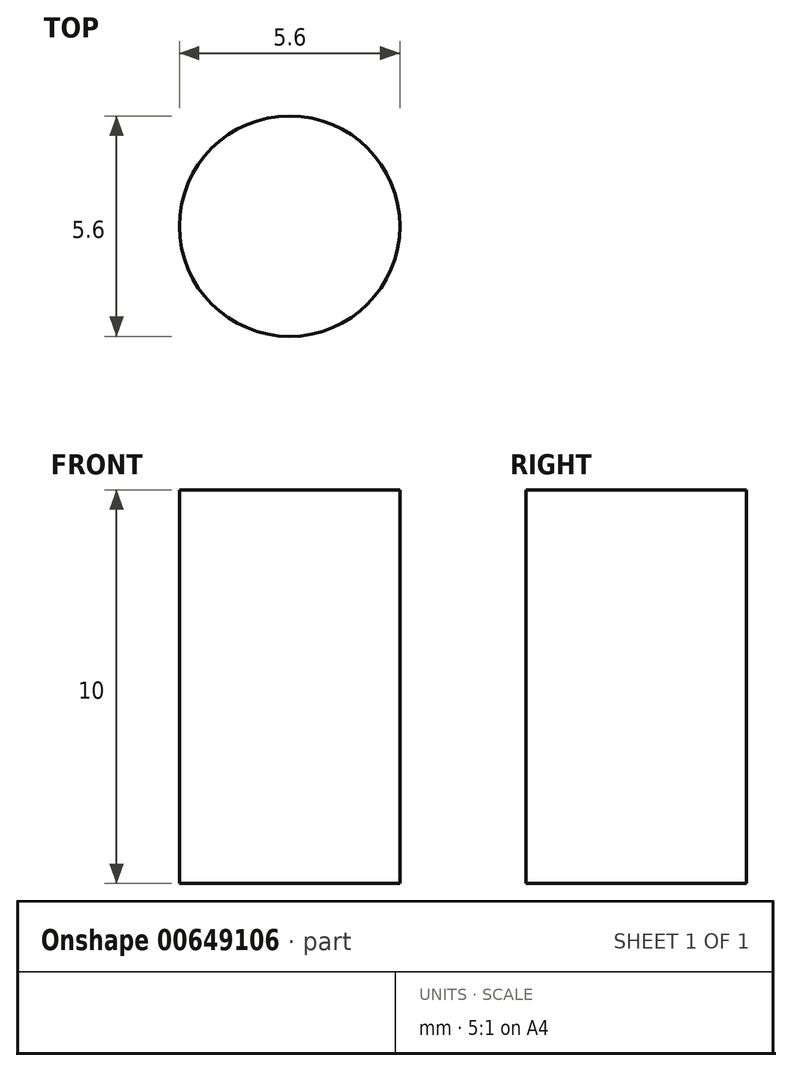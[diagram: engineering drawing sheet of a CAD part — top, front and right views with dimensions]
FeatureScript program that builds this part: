
annotation { "Feature Type Name" : "Feature", "Feature Type Description" : "" }
export const myFeature = defineFeature(function(context is Context, id is Id, definition is map)
    precondition{}
    {
        {
            var Q0;
            Q0=qCreatedBy(makeId("Top.planeOp"),FACE);
            var sketch = newSketch(context, id + "F0", { "sketchPlane" : qUnion([Q0])});
            skCircle(sketch, "E0", {"center": v(0, 0) * mm, "radius": 2.8 * mm});
            skSolve(sketch);
        }
        {
            var Q0;
            Q0=makeQuery(id+"F0.imprint","IMPRINT",FACE,{"disambiguationData":[TD([[makeQuery(id+"F0.imprint","IMPRINT",EDGE,{"derivedFrom":sQuery(id+"F0.wireOp",EDGE,"E0")}),1.0]])]});
            extrude(context, id + "F1", {"entities" : qUnion([Q0]), "depth" : 10 * mm, "offsetDistance" : 25 * mm});
        }
    });
